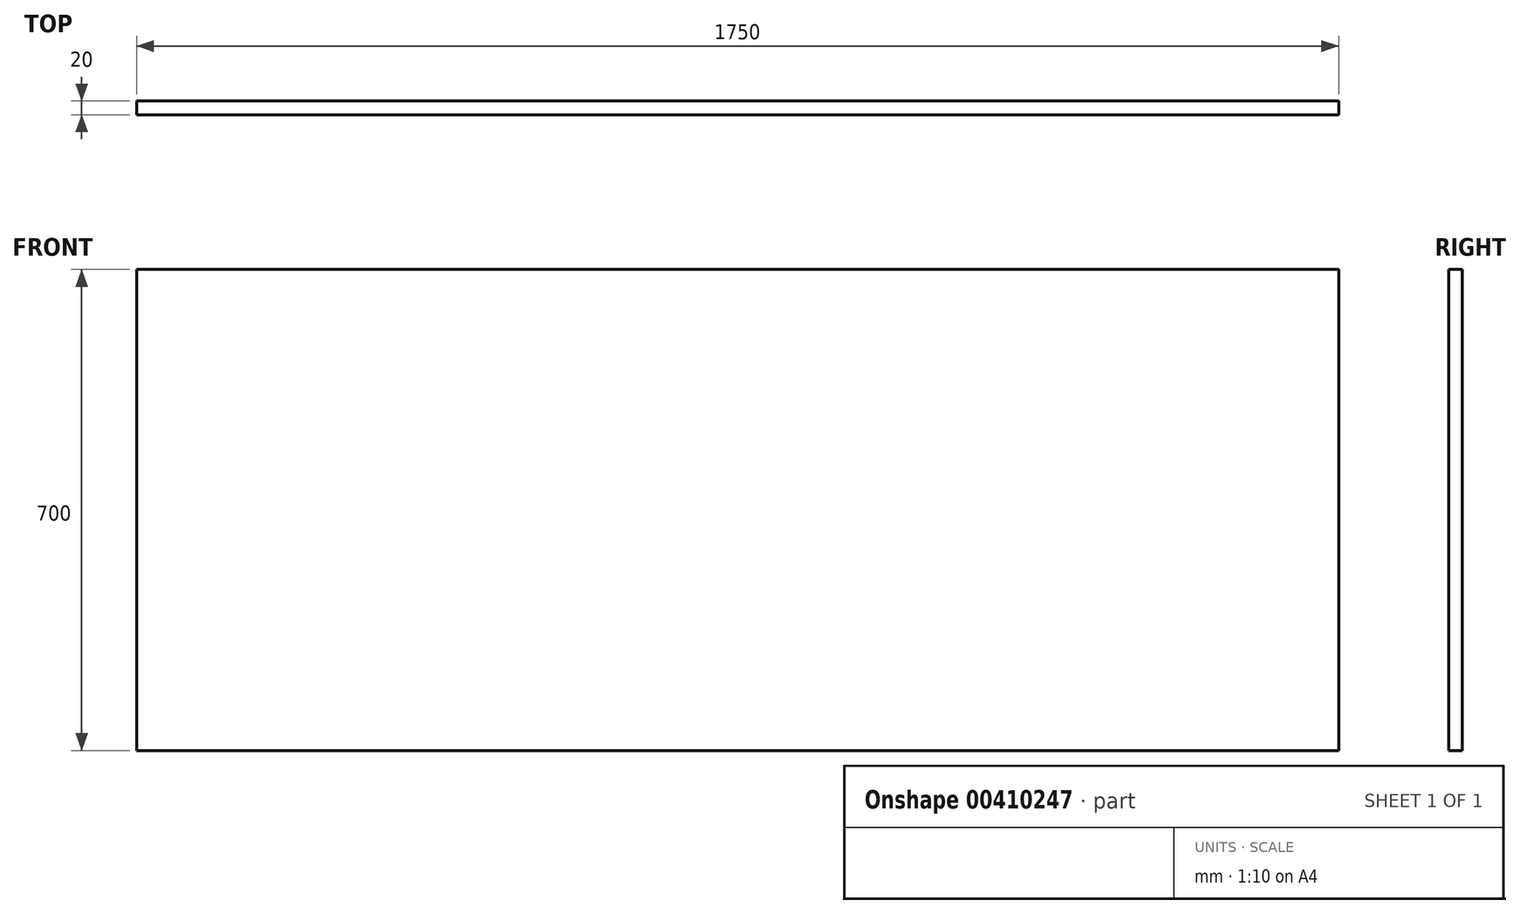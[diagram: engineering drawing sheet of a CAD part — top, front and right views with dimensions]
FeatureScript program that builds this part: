
annotation { "Feature Type Name" : "Feature", "Feature Type Description" : "" }
export const myFeature = defineFeature(function(context is Context, id is Id, definition is map)
    precondition{}
    {
        {
            var Q0;
            Q0=qCreatedBy(makeId("Front.planeOp"),FACE);
            var sketch = newSketch(context, id + "F0", { "sketchPlane" : qUnion([Q0])});
            skLineSegment(sketch, "E0.bottom", {"start": v(-875, 350) * mm, "end": v(875, 350) * mm});
            skLineSegment(sketch, "E0.top", {"start": v(-875, -350) * mm, "end": v(875, -350) * mm});
            skLineSegment(sketch, "E0.left", {"start": v(-875, 350) * mm, "end": v(-875, -350) * mm});
            skLineSegment(sketch, "E0.right", {"start": v(875, 350) * mm, "end": v(875, -350) * mm});
            skPoint(sketch, "E0.middle", {"position": v(0, 0) * mm});
            skSolve(sketch);
        }
        {
            var Q0;
            Q0=makeQuery(id+"F0.imprint","IMPRINT",FACE,{"disambiguationData":[TD([[makeQuery(id+"F0.imprint","IMPRINT",EDGE,{"derivedFrom":sQuery(id+"F0.wireOp",EDGE,"E0.bottom")}),-1.0]])]});
            extrude(context, id + "F1", {"entities" : qUnion([Q0]), "flatOperationType" : FlatOperationType.REMOVE, "endBound" : BoundingType.SYMMETRIC, "offsetDistance" : 25 * mm, "depth" : 20 * mm, "domain" : OperationDomain.MODEL});
        }
    });
